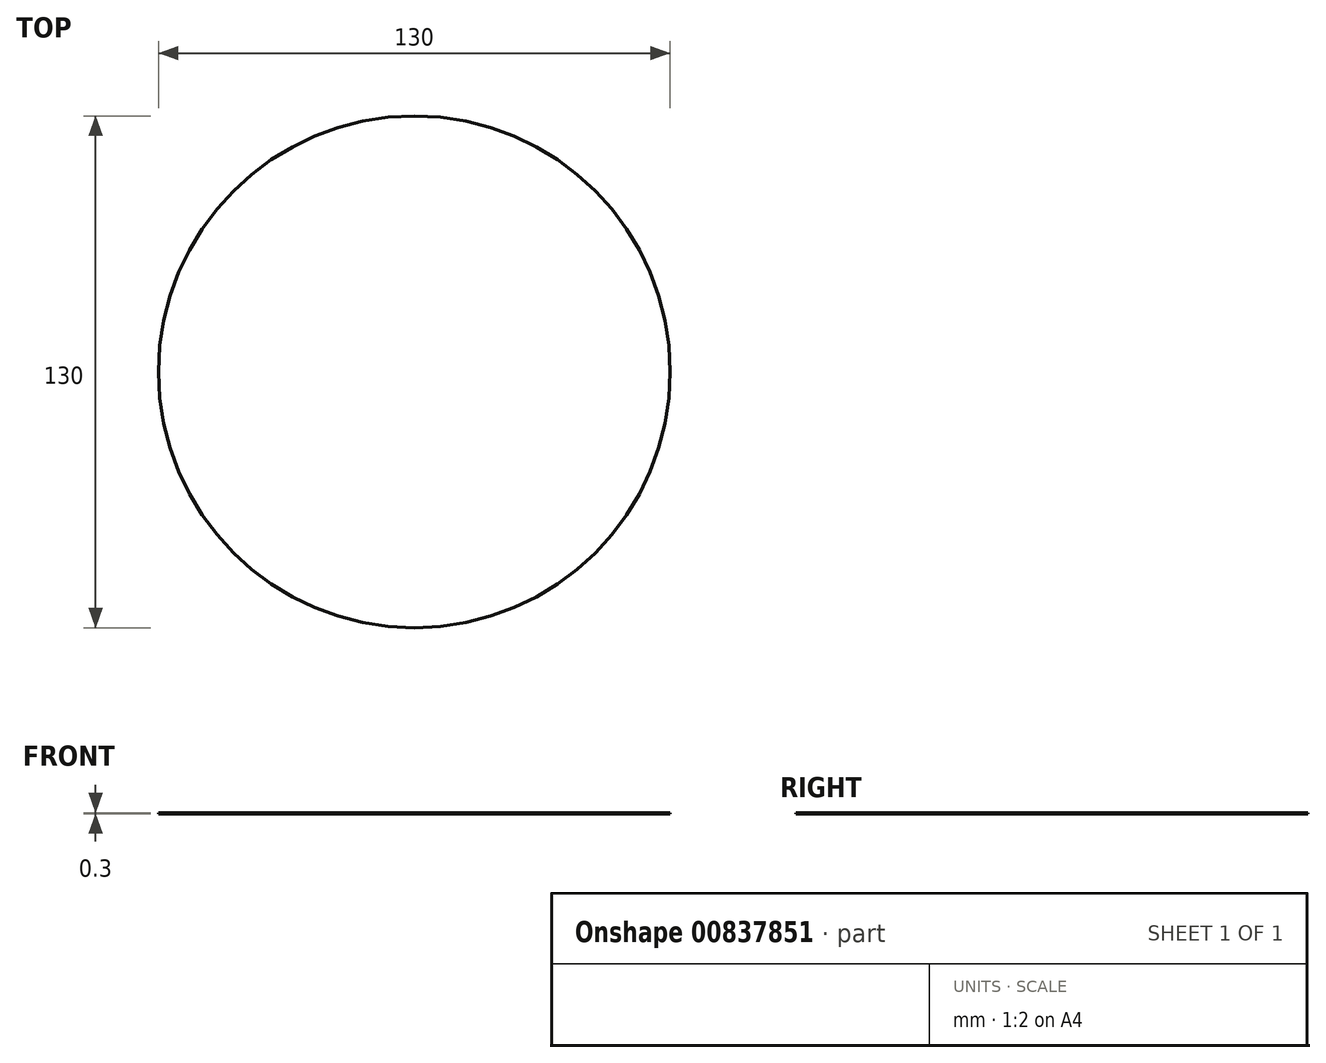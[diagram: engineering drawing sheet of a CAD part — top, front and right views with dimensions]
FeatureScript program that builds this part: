
annotation { "Feature Type Name" : "Feature", "Feature Type Description" : "" }
export const myFeature = defineFeature(function(context is Context, id is Id, definition is map)
    precondition{}
    {
        {
            var Q0;
            Q0=qCreatedBy(makeId("Top.planeOp"),FACE);
            var sketch = newSketch(context, id + "F0", { "sketchPlane" : qUnion([Q0])});
            skCircle(sketch, "E0", {"center": v(0, 0) * mm, "radius": 65 * mm});
            skSolve(sketch);
        }
        {
            var Q0;
            Q0=makeQuery(id+"F0.imprint","IMPRINT",FACE,{"disambiguationData":[TD([[makeQuery(id+"F0.imprint","IMPRINT",EDGE,{"derivedFrom":sQuery(id+"F0.wireOp",EDGE,"E0")}),1.0]])]});
            extrude(context, id + "F1", {"entities" : qUnion([Q0]), "depth" : .3 * mm, "offsetDistance" : 25 * mm});
        }
    });
